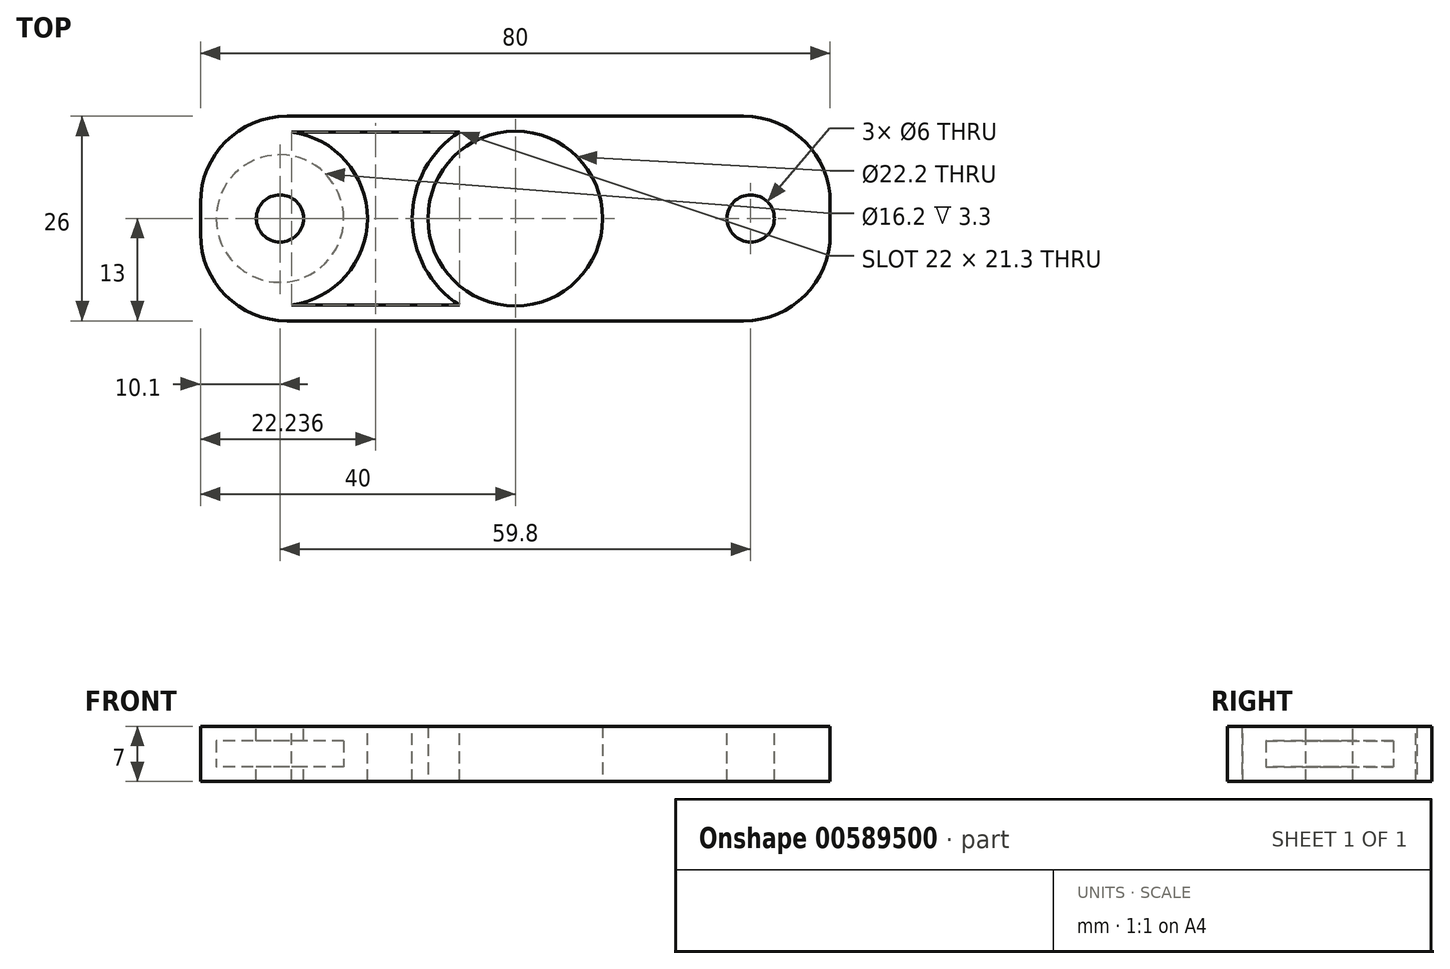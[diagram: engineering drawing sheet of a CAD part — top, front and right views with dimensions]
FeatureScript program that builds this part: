
annotation { "Feature Type Name" : "Feature", "Feature Type Description" : "" }
export const myFeature = defineFeature(function(context is Context, id is Id, definition is map)
    precondition{}
    {
        {
            var Q0;
            Q0=qCreatedBy(makeId("Top.planeOp"),FACE);
            var sketch = newSketch(context, id + "F0", { "sketchPlane" : qUnion([Q0])});
            skCircle(sketch, "E0", {"center": v(0, 0) * mm, "radius": 11.1 * mm});
            skLineSegment(sketch, "E1.bottom", {"start": v(29, 13) * mm, "end": v(-29, 13) * mm});
            skLineSegment(sketch, "E1.top", {"start": v(29, -13) * mm, "end": v(-29, -13) * mm});
            skLineSegment(sketch, "E1.left", {"start": v(40, 2) * mm, "end": v(40, -2) * mm});
            skLineSegment(sketch, "E1.right", {"start": v(-40, 2) * mm, "end": v(-40, -2) * mm});
            skPoint(sketch, "E2.visualSharp", {"position": v(-40, 13) * mm});
            skArc(sketch, "E2.filletArc", {"start": v(-29, 13) * mm, "mid": v(-36.78, 9.78) * mm, "end": v(-40, 2) * mm});
            skPoint(sketch, "E3.visualSharp", {"position": v(-40, -13) * mm});
            skArc(sketch, "E3.filletArc", {"start": v(-40, -2) * mm, "mid": v(-36.78, -9.78) * mm, "end": v(-29, -13) * mm});
            skPoint(sketch, "E4.visualSharp", {"position": v(40, -13) * mm});
            skArc(sketch, "E4.filletArc", {"start": v(29, -13) * mm, "mid": v(36.78, -9.78) * mm, "end": v(40, -2) * mm});
            skPoint(sketch, "E5.visualSharp", {"position": v(40, 13) * mm});
            skArc(sketch, "E5.filletArc", {"start": v(40, 2) * mm, "mid": v(36.78, 9.78) * mm, "end": v(29, 13) * mm});
            skSolve(sketch);
        }
        {
            var Q0;
            Q0 = qSketchRegion(id + "F0", true);
            extrude(context, id + "F1", {"entities" : qUnion([Q0]), "endBound" : BoundingType.SYMMETRIC, "depth" : 7 * mm, "offsetDistance" : 25 * mm});
        }
        {
            var Q0;
            Q0=qCreatedBy(makeId("Top.planeOp"),FACE);
            var sketch = newSketch(context, id + "F2", { "sketchPlane" : qUnion([Q0])});
            skCircle(sketch, "E6", {"center": v(-29.9, 0) * mm, "radius": 8.1 * mm});
            skSolve(sketch);
        }
        {
            assignVariable(context, id + "F3", {"name" : "eRondelle", "anyValue" : 1.1});
        }
        {
            var Q0;
            Q0 = qSketchRegion(id + "F2", true);
            extrude(context, id + "F4", {"entities" : qUnion([Q0]), "operationType" : NewBodyOperationType.REMOVE, "endBound" : BoundingType.SYMMETRIC, "depth" : (3 * getVariable(context, 'eRondelle')) * mm, "offsetDistance" : 25 * mm});
        }
        {
            var Q0;
            Q0=makeQuery(id+"F1.opExtrude","CAP_FACE",FACE,{"disambiguationData":[OSD([sQuery(id+"F0.wireOp",EDGE,"E0"),sQuery(id+"F0.wireOp",EDGE,"E1.bottom"),sQuery(id+"F0.wireOp",EDGE,"E1.top"),sQuery(id+"F0.wireOp",EDGE,"E1.left"),sQuery(id+"F0.wireOp",EDGE,"E1.right"),sQuery(id+"F0.wireOp",EDGE,"E2.filletArc"),sQuery(id+"F0.wireOp",EDGE,"E3.filletArc"),sQuery(id+"F0.wireOp",EDGE,"E4.filletArc"),sQuery(id+"F0.wireOp",EDGE,"E5.filletArc")])],"isStart":false});
            var sketch = newSketch(context, id + "F5", { "sketchPlane" : qUnion([Q0])});
            skLineSegment(sketch, "E7.0", {"start": v(29, 11) * mm, "end": v(-28.41, 11) * mm});
            skCircle(sketch, "E8.0", {"center": v(-29.9, 0) * mm, "radius": 11.1 * mm});
            skCircle(sketch, "E9.0", {"center": v(0, 0) * mm, "radius": 13.1 * mm});
            skLineSegment(sketch, "E10.0", {"start": v(29, -11) * mm, "end": v(-28.41, -11) * mm});
            skPoint(sketch, "E11", {"position": v(-7.11, -11) * mm});
            skPoint(sketch, "E12", {"position": v(-7.75, -30.2) * mm});
            skPoint(sketch, "E13", {"position": v(-7.11, 11) * mm});
            skSolve(sketch);
        }
        {
            var Q0;
            {var subQ0=sQuery(id+"F5.wireOp",EDGE,"E8.0");var subQ1=sQuery(id+"F5.wireOp",EDGE,"E7.0");var subQ2=makeQuery(id+"F5.imprint","INTERSECT",VERTEX,{"derivedFrom":[subQ1,subQ0]});Q0=makeQuery(id+"F5.imprint","IMPRINT",FACE,{"disambiguationData":[TD([[makeQuery(id+"F5.imprint","IMPRINT",EDGE,{"disambiguationData":[TD([[subQ2,1.0]])],"derivedFrom":subQ1}),1.0]])]});}
            extrude(context, id + "F6", {"entities" : qUnion([Q0]), "operationType" : NewBodyOperationType.REMOVE, "endBound" : BoundingType.THROUGH_ALL, "oppositeDirection" : true, "depth" : 25 * mm, "offsetDistance" : 25 * mm});
        }
        {
            var Q0;
            Q0=makeQuery(id+"F1.opExtrude","CAP_FACE",FACE,{"disambiguationData":[OSD([sQuery(id+"F0.wireOp",EDGE,"E0"),sQuery(id+"F0.wireOp",EDGE,"E1.bottom"),sQuery(id+"F0.wireOp",EDGE,"E1.top"),sQuery(id+"F0.wireOp",EDGE,"E1.left"),sQuery(id+"F0.wireOp",EDGE,"E1.right"),sQuery(id+"F0.wireOp",EDGE,"E2.filletArc"),sQuery(id+"F0.wireOp",EDGE,"E3.filletArc"),sQuery(id+"F0.wireOp",EDGE,"E4.filletArc"),sQuery(id+"F0.wireOp",EDGE,"E5.filletArc")])],"isStart":false});
            var sketch = newSketch(context, id + "F7", { "sketchPlane" : qUnion([Q0])});
            skCircle(sketch, "E14.0", {"center": v(29.9, 0) * mm, "radius": 8.1 * mm, "construction": true});
            skCircle(sketch, "E15", {"center": v(29.9, 0) * mm, "radius": 3 * mm});
            skLineSegment(sketch, "E16", {"start": v(0, 22.9) * mm, "end": v(0, -23) * mm, "construction": true});
            skPoint(sketch, "E16.endSnap0", {"position": v(0, -13) * mm});
            skCircle(sketch, "E17.MirrorC", {"center": v(-29.9, 0) * mm, "radius": 3 * mm});
            skSolve(sketch);
        }
        {
            var Q0;
            Q0 = qSketchRegion(id + "F7", true);
            extrude(context, id + "F8", {"entities" : qUnion([Q0]), "operationType" : NewBodyOperationType.REMOVE, "endBound" : BoundingType.THROUGH_ALL, "oppositeDirection" : true, "depth" : 25 * mm, "offsetDistance" : 25 * mm});
        }
        {
            var Q0;
            Q0=makeQuery(id+"F1.opExtrude","CAP_FACE",FACE,{"disambiguationData":[OSD([sQuery(id+"F0.wireOp",EDGE,"E0"),sQuery(id+"F0.wireOp",EDGE,"E1.bottom"),sQuery(id+"F0.wireOp",EDGE,"E1.top"),sQuery(id+"F0.wireOp",EDGE,"E1.left"),sQuery(id+"F0.wireOp",EDGE,"E1.right"),sQuery(id+"F0.wireOp",EDGE,"E2.filletArc"),sQuery(id+"F0.wireOp",EDGE,"E3.filletArc"),sQuery(id+"F0.wireOp",EDGE,"E4.filletArc"),sQuery(id+"F0.wireOp",EDGE,"E5.filletArc")])],"isStart":false});
            var sketch = newSketch(context, id + "F9", { "sketchPlane" : qUnion([Q0])});
            skCircle(sketch, "E18.0", {"center": v(29.9, 0) * mm, "radius": 3 * mm});
            skCircle(sketch, "E19", {"center": v(29.9, 0) * mm, "radius": 3.88 * mm});
            skSolve(sketch);
        }
        {
            var Q0;
            Q0 = qSketchRegion(id + "F9", true);
            var Q1;
            Q1=makeQuery(id+"F1.opExtrude","CAP_FACE",FACE,{"disambiguationData":[OSD([sQuery(id+"F0.wireOp",EDGE,"E0"),sQuery(id+"F0.wireOp",EDGE,"E1.bottom"),sQuery(id+"F0.wireOp",EDGE,"E1.top"),sQuery(id+"F0.wireOp",EDGE,"E1.left"),sQuery(id+"F0.wireOp",EDGE,"E1.right"),sQuery(id+"F0.wireOp",EDGE,"E2.filletArc"),sQuery(id+"F0.wireOp",EDGE,"E3.filletArc"),sQuery(id+"F0.wireOp",EDGE,"E4.filletArc"),sQuery(id+"F0.wireOp",EDGE,"E5.filletArc")])],"isStart":true});
            extrude(context, id + "F10", {"entities" : qUnion([Q0]), "operationType" : NewBodyOperationType.ADD, "endBound" : BoundingType.UP_TO_SURFACE, "oppositeDirection" : true, "depth" : 25 * mm, "endBoundEntityFace" : qUnion([Q1]), "offsetDistance" : 25 * mm});
        }
    });
